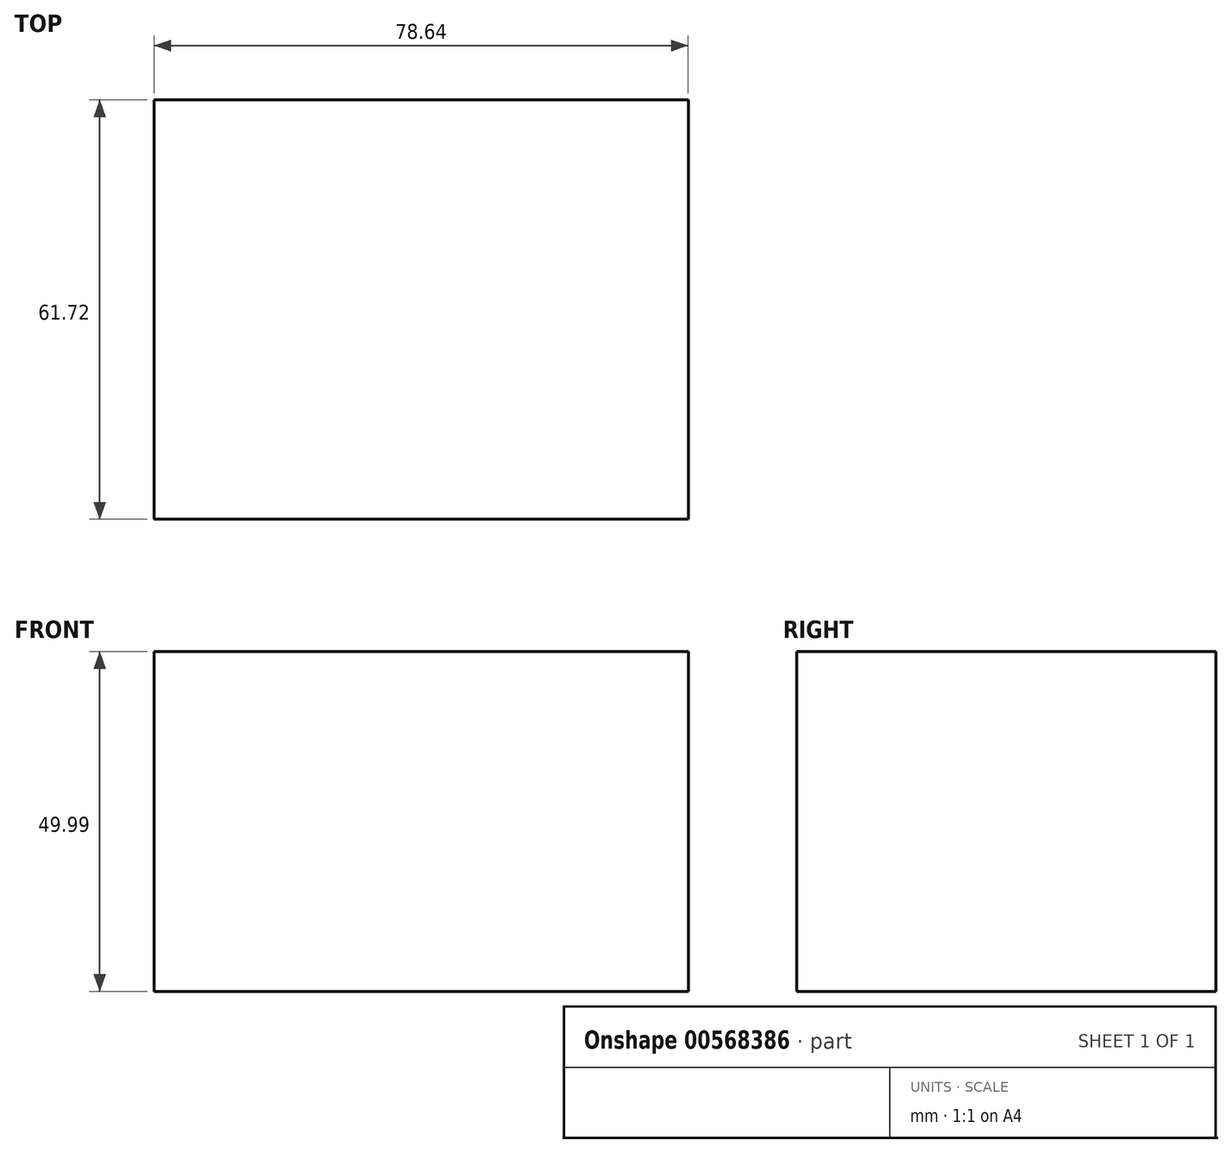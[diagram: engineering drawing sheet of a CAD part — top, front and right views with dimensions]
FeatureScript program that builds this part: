
annotation { "Feature Type Name" : "Feature", "Feature Type Description" : "" }
export const myFeature = defineFeature(function(context is Context, id is Id, definition is map)
    precondition{}
    {
        {
            var Q0;
            Q0=qCreatedBy(makeId("Front.planeOp"),FACE);
            var sketch = newSketch(context, id + "F0", { "sketchPlane" : qUnion([Q0])});
            skLineSegment(sketch, "E0.bottom", {"start": v(-37.8, 31.85) * mm, "end": v(40.84, 31.85) * mm});
            skLineSegment(sketch, "E0.top", {"start": v(-37.8, -18.14) * mm, "end": v(40.84, -18.14) * mm});
            skLineSegment(sketch, "E0.left", {"start": v(-37.8, 31.85) * mm, "end": v(-37.8, -18.14) * mm});
            skLineSegment(sketch, "E0.right", {"start": v(40.84, 31.85) * mm, "end": v(40.84, -18.14) * mm});
            skSolve(sketch);
        }
        {
            var Q0;
            Q0=makeQuery(id+"F0.imprint","IMPRINT",FACE,{"disambiguationData":[TD([[makeQuery(id+"F0.imprint","IMPRINT",EDGE,{"derivedFrom":sQuery(id+"F0.wireOp",EDGE,"E0.bottom")}),-1.0]])]});
            extrude(context, id + "F1", {"entities" : qUnion([Q0]), "depth" : 61.72 * mm, "offsetDistance" : 25.4 * mm});
        }
    });
